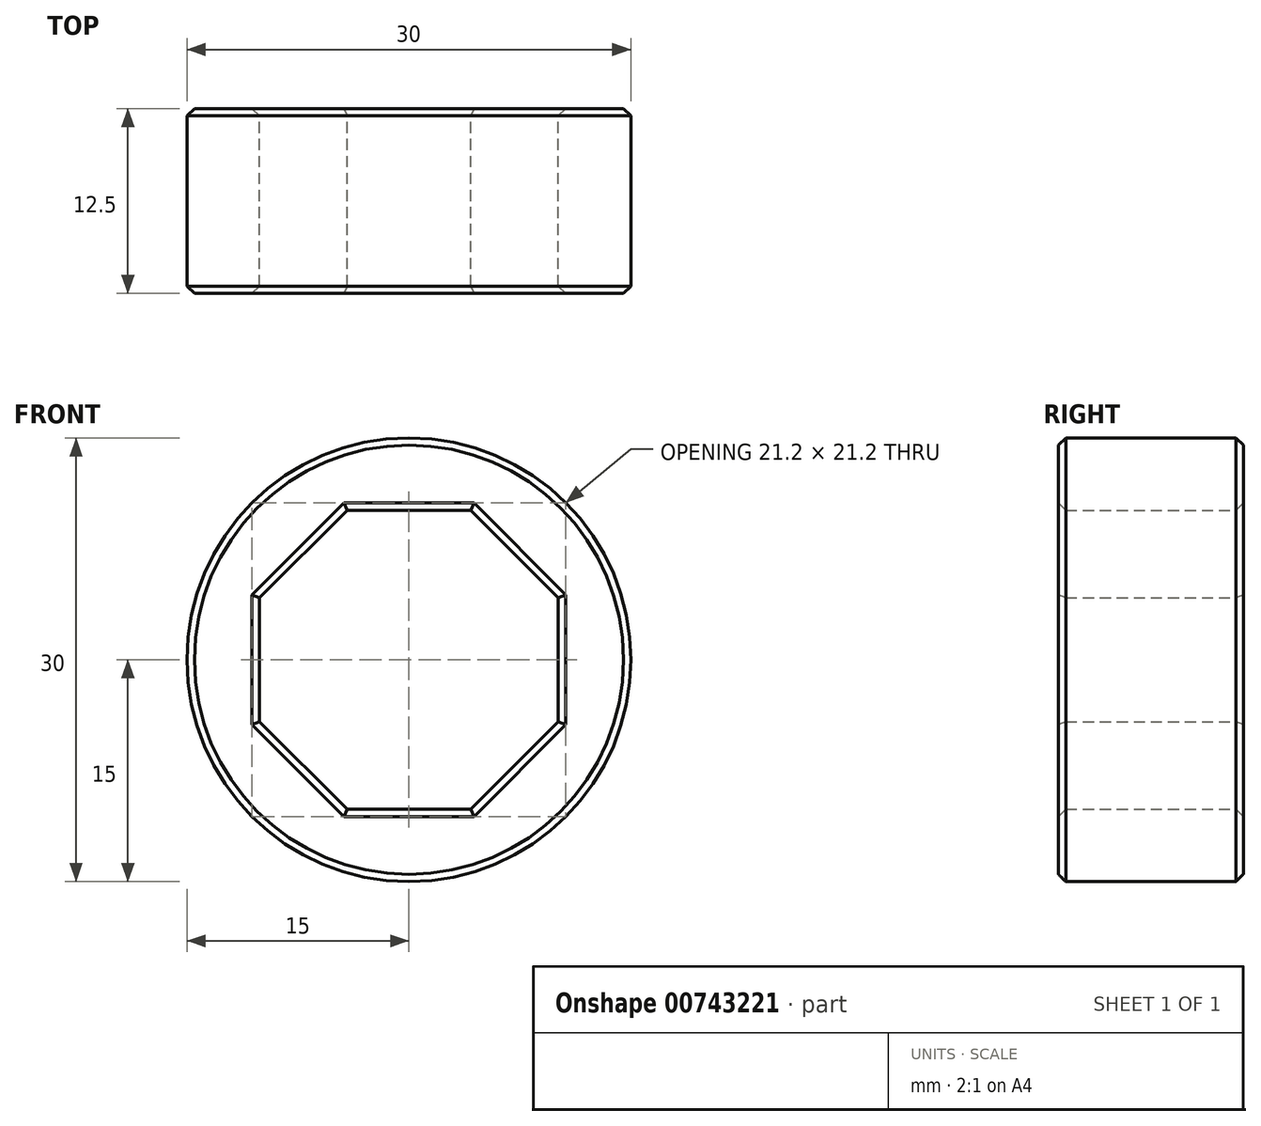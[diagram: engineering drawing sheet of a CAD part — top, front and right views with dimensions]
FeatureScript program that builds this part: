
annotation { "Feature Type Name" : "Feature", "Feature Type Description" : "" }
export const myFeature = defineFeature(function(context is Context, id is Id, definition is map)
    precondition{}
    {
        {
            var Q0;
            Q0=qCreatedBy(makeId("Front.planeOp"),FACE);
            var sketch = newSketch(context, id + "F0", { "sketchPlane" : qUnion([Q0])});
            skCircle(sketch, "E0", {"center": v(0, 0) * mm, "radius": 15 * mm});
            skCircle(sketch, "E1.cCircle", {"center": v(0, 0) * mm, "radius": 10.1 * mm, "construction": true});
            skLineSegment(sketch, "E1.0", {"start": v(-10.1, -4.18) * mm, "end": v(-10.1, 4.18) * mm});
            skLineSegment(sketch, "E1.1", {"start": v(-10.1, 4.18) * mm, "end": v(-4.18, 10.1) * mm});
            skLineSegment(sketch, "E1.2", {"start": v(-4.18, 10.1) * mm, "end": v(4.18, 10.1) * mm});
            skLineSegment(sketch, "E1.3", {"start": v(4.18, 10.1) * mm, "end": v(10.1, 4.18) * mm});
            skLineSegment(sketch, "E1.4", {"start": v(10.1, 4.18) * mm, "end": v(10.1, -4.18) * mm});
            skLineSegment(sketch, "E1.5", {"start": v(10.1, -4.18) * mm, "end": v(4.18, -10.1) * mm});
            skLineSegment(sketch, "E1.6", {"start": v(4.18, -10.1) * mm, "end": v(-4.18, -10.1) * mm});
            skLineSegment(sketch, "E1.7", {"start": v(-4.18, -10.1) * mm, "end": v(-10.1, -4.18) * mm});
            skPoint(sketch, "E1.0.midPoint", {"position": v(-10.1, 0) * mm});
            skSolve(sketch);
        }
        {
            var Q0;
            Q0=makeQuery(id+"F0.imprint","IMPRINT",FACE,{"disambiguationData":[TD([[makeQuery(id+"F0.imprint","IMPRINT",EDGE,{"derivedFrom":sQuery(id+"F0.wireOp",EDGE,"E0")}),1.0]])]});
            var Q1;
            Q1=sQuery(id+"F0.wireOp",EDGE,"E0");
            extrude(context, id + "F1", {"entities" : qUnion([Q0]), "surfaceEntities" : qUnion([Q1]), "depth" : 12.5 * mm, "offsetDistance" : 25 * mm});
        }
        {
            var Q0;
            Q0=makeQuery(id+"F1.opExtrude","CAP_FACE",FACE,{"disambiguationData":[OSD([sQuery(id+"F0.wireOp",EDGE,"E0"),sQuery(id+"F0.wireOp",EDGE,"E1.0"),sQuery(id+"F0.wireOp",EDGE,"E1.1"),sQuery(id+"F0.wireOp",EDGE,"E1.2"),sQuery(id+"F0.wireOp",EDGE,"E1.3"),sQuery(id+"F0.wireOp",EDGE,"E1.4"),sQuery(id+"F0.wireOp",EDGE,"E1.5"),sQuery(id+"F0.wireOp",EDGE,"E1.6"),sQuery(id+"F0.wireOp",EDGE,"E1.7")])],"isStart":false});
            var Q1;
            Q1=makeQuery(id+"F1.opExtrude","CAP_FACE",FACE,{"disambiguationData":[OSD([sQuery(id+"F0.wireOp",EDGE,"E0"),sQuery(id+"F0.wireOp",EDGE,"E1.0"),sQuery(id+"F0.wireOp",EDGE,"E1.1"),sQuery(id+"F0.wireOp",EDGE,"E1.2"),sQuery(id+"F0.wireOp",EDGE,"E1.3"),sQuery(id+"F0.wireOp",EDGE,"E1.4"),sQuery(id+"F0.wireOp",EDGE,"E1.5"),sQuery(id+"F0.wireOp",EDGE,"E1.6"),sQuery(id+"F0.wireOp",EDGE,"E1.7")])],"isStart":true});
            chamfer(context, id + "F2", {"entities" : qUnion([Q0, Q1]), "width" : 0.5 * mm, "tangentPropagation" : true});
        }
    });
